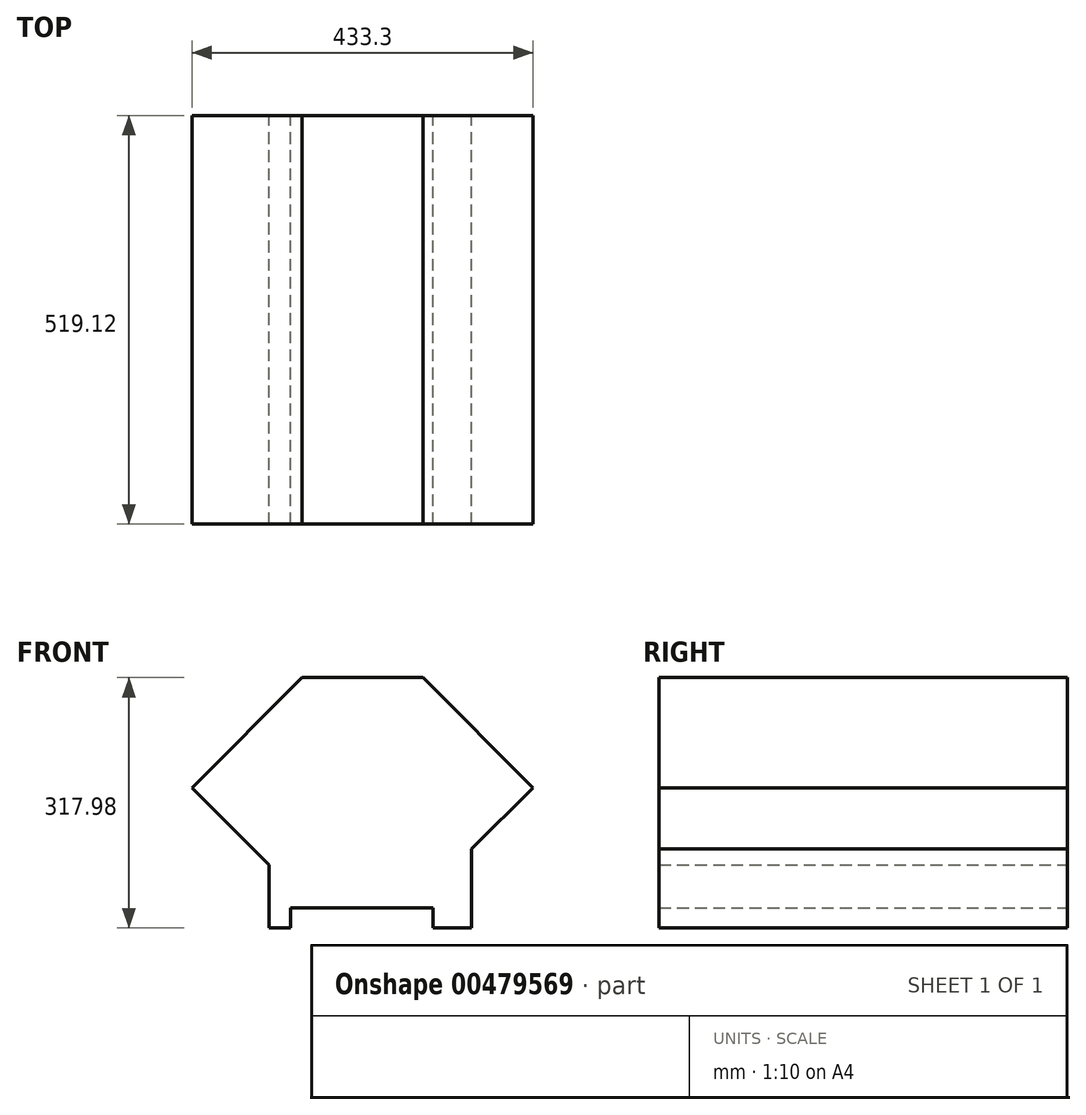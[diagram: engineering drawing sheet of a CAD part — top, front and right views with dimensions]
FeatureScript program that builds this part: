
annotation { "Feature Type Name" : "Feature", "Feature Type Description" : "" }
export const myFeature = defineFeature(function(context is Context, id is Id, definition is map)
    precondition{}
    {
        {
            var Q0;
            Q0=qCreatedBy(makeId("Front.planeOp"),FACE);
            var sketch = newSketch(context, id + "F0", { "sketchPlane" : qUnion([Q0])});
            skLineSegment(sketch, "E0", {"start": v(-78.1, 158.2) * mm, "end": v(75.7, 158.2) * mm});
            skLineSegment(sketch, "E1", {"start": v(-78.1, 158.2) * mm, "end": v(-217.85, 18.44) * mm});
            skLineSegment(sketch, "E2", {"start": v(75.7, 158.2) * mm, "end": v(215.45, 18.45) * mm});
            skLineSegment(sketch, "E3", {"start": v(-217.85, 18.44) * mm, "end": v(-119.95, -79.45) * mm});
            skLineSegment(sketch, "E4", {"start": v(-119.95, -79.45) * mm, "end": v(-119.95, -159.78) * mm});
            skLineSegment(sketch, "E5", {"start": v(215.45, 18.45) * mm, "end": v(137.67, -59.33) * mm});
            skLineSegment(sketch, "E6", {"start": v(137.67, -59.33) * mm, "end": v(137.67, -159.66) * mm});
            skLineSegment(sketch, "E7", {"start": v(-119.95, -159.78) * mm, "end": v(-92.31, -159.78) * mm});
            skLineSegment(sketch, "E8", {"start": v(-92.31, -159.78) * mm, "end": v(-92.31, -134.38) * mm});
            skLineSegment(sketch, "E9", {"start": v(-92.31, -134.38) * mm, "end": v(88.45, -134.38) * mm});
            skLineSegment(sketch, "E10", {"start": v(88.45, -134.38) * mm, "end": v(88.45, -159.78) * mm});
            skLineSegment(sketch, "E11", {"start": v(88.45, -159.78) * mm, "end": v(137.67, -159.66) * mm});
            skSolve(sketch);
        }
        {
            var Q0;
            Q0 = qSketchRegion(id + "F0", true);
            extrude(context, id + "F1", {"entities" : qUnion([Q0]), "endBound" : BoundingType.SYMMETRIC, "depth" : 519.1 * mm});
        }
    });
